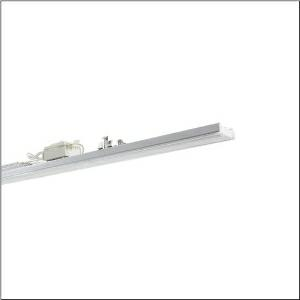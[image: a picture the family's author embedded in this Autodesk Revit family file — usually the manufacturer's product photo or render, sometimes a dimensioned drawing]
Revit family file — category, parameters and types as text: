
# Revit family: licross_r__21_recessed_mo_52tl12dn4axgd_376d
name_source: partatom
category: Lighting Fixtures
units: mm (PartAtom-declared; Revit-internal decimal feet)

## family parameters
Cut with Voids When Loaded = No
Host = Face
Light Source = No
Part Type = Normal
Room Calculation Point = No
Round Connector Dimension = Use Diameter
Shared = No

## types (1)
- --- (1 x LED, 1540 lm, 9.7 W, 4000K)
    Apparent Load = 10 VA
    CIE Flux Codes = 72 92 99 100 100
    Color Rendering = 80
    Color Temperature = 4000K
    Default Elevation = 1800 mm
    Description = Licross® 21 Recessed MO, luminaire insert, of sheet steel, galvanised, coil coated, white, length: 1.500mm, width: 66mm, height: 67mm, LED rated luminous flux: 10.280lm, light colour: 840, control gear: DALI 2 (for two DALI lines), with plug, 6-pole, with phase selection, mains connection: 220..240V, AC/DC, 0/50..60Hz, rated input power: 58W, without changeover relay, for emergency light function, for central battery installations according to DIN EN 60598-2-22, internal wiring halogen-free, primary optical cover: cover, of PMMA, light emission: direct distribution, primary light characteristic: symmetric, protection rating (complete): IP40, insulation class (complete): insulation class I (protective earthing), certification: CE, ENEC, VDE, UKCA, protection symbol: D if used in an environment without relevant dust loads with corresponding accessories, impact resistance: IK06, permissible ambient temperature for indoor applications: -25..+35°C, standard: EN 60598-2-22, corresponds to IFS (International Featured Standards) requirements for safety and quality in the food industry, reducing of maximum allowable ambient temperature of 5°C with ceiling mounting, LABS conformity tested according to VDMA 24364:2018-05, packaging unit: 1 piece
    Height = 58 mm
    Lamp = 1 x LED
    Lamp Light Flux = 1540 lm
    Lamp Power = 9.7 W
    Lamp count = 1
    Length = 1500 mm
    Luminous efficacy = 159 lm/W
    Manufacturer = Siteco
    ModVariant = No
    Model = 52TL12DN4AXGD
    Mounting Place = Ceiling
    Mounting Type = Pendant
    Number of Poles = 1
    OnlyDefault = Yes
    Power Factor = 1
    Product Name = Licross® 21 Recessed MO
    Product group = luminaire insert | ceiling pendant
    ProductGroupID = 902
    Protection Class = Protection class I
    Protection Degree = IP 40
    RLX_Detail_Level = 1
    RLX_Emergency_Light_Flux = 0 lm
    RLX_Emergency_Type = 0
    RLX_Emergency_Type_DB = No
    RlxData = <blob elided: 25181 chars, md5=78db7f31>
    Socket = socket
    Standby Power = 0 W
    System Light Flux = 1540 lm
    System Power = 10 W
    Type Comments = : DC mode (central or group accumulator) initial emergency light level
    Type Image = l_1296930.jpg
    URL = http://relux.com
    VarID = @adj_134627
    Voltage = 0 V
    Weight = 0.00 kg
    Width = 66 mm

## geometry (parser evidence)
native form markers: Blend x4, Sweep x11
no freeform markers — native parametric forms only
